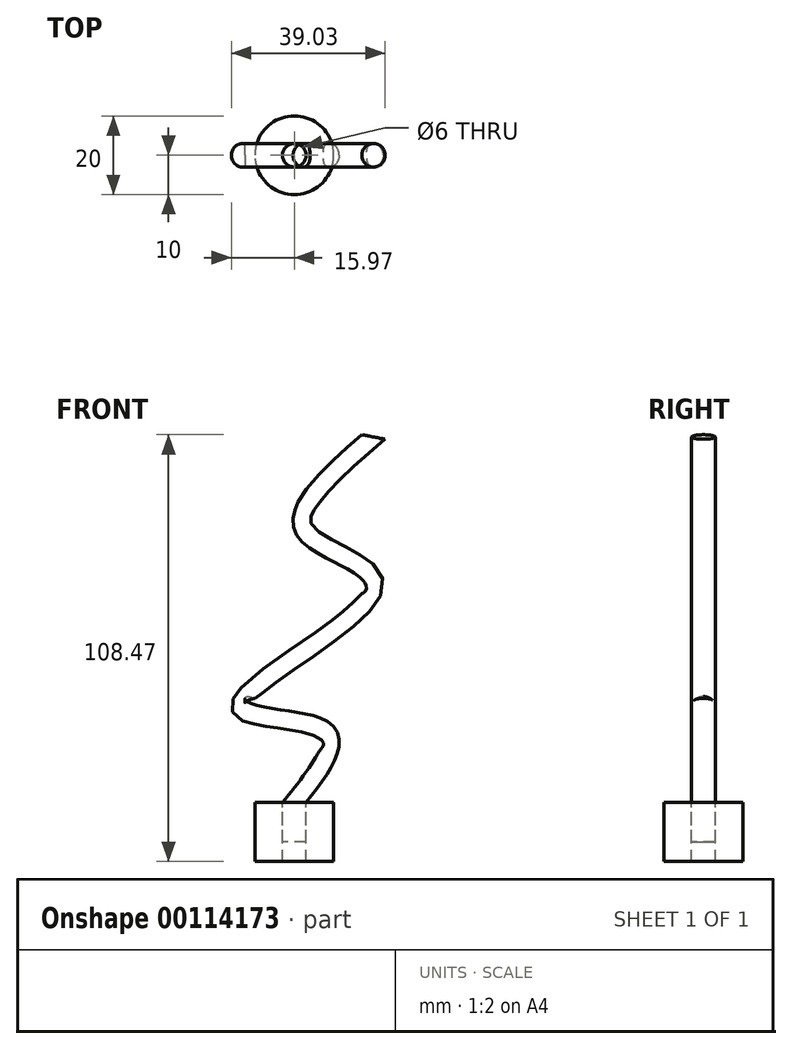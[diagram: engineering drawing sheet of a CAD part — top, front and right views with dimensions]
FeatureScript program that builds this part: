
annotation { "Feature Type Name" : "Feature", "Feature Type Description" : "" }
export const myFeature = defineFeature(function(context is Context, id is Id, definition is map)
    precondition{}
    {
        {
            var Q0;
            Q0=qCreatedBy(makeId("Top.planeOp"),FACE);
            var sketch = newSketch(context, id + "F0", { "sketchPlane" : qUnion([Q0])});
            skCircle(sketch, "E0", {"center": v(0, 0) * mm, "radius": 10 * mm});
            skCircle(sketch, "E1", {"center": v(0, 0) * mm, "radius": 3 * mm});
            skSolve(sketch);
        }
        {
            var Q0;
            Q0=qCreatedBy(makeId("Front.planeOp"),FACE);
            var sketch = newSketch(context, id + "F1", { "sketchPlane" : qUnion([Q0])});
            skFitSpline(sketch, "E2", {"points": [v(0, 0) * mm, v(7.33, 18.22) * mm, v(-13.25, 24.8) * mm, v(19.97, 54.7) * mm, v(3.1, 68.86) * mm, v(20.11, 92.9) * mm], "startDerivative": vector(102.5, 129.99) * mm, "endDerivative": vector(150.44, 129.38) * mm});
            skSolve(sketch);
        }
        {
            var Q0;
            Q0=makeQuery(id+"F0.imprint","IMPRINT",FACE,{"disambiguationData":[TD([[makeQuery(id+"F0.imprint","IMPRINT",EDGE,{"derivedFrom":sQuery(id+"F0.wireOp",EDGE,"E1")}),1.0]])]});
            var Q1;
            Q1=sQuery(id+"F1.wireOp",EDGE,"E2");
            sweep(context, id + "F2", {"profiles" : qUnion([Q0]), "path" : qUnion([Q1])});
        }
        {
            var Q0;
            Q0=makeQuery(id+"F0.imprint","IMPRINT",FACE,{"disambiguationData":[TD([[makeQuery(id+"F0.imprint","IMPRINT",EDGE,{"derivedFrom":sQuery(id+"F0.wireOp",EDGE,"E0")}),1.0]])]});
            extrude(context, id + "F3", {"entities" : qUnion([Q0]), "operationType" : NewBodyOperationType.ADD, "oppositeDirection" : true, "depth" : 15 * mm});
        }
        {
            var Q0;
            Q0=makeQuery(id+"F2.opSweep","CAP_FACE",FACE,{"disambiguationData":[OSD([sQuery(id+"F0.wireOp",EDGE,"E1"),sQuery(id+"F1.wireOp",VERTEX,"E2.start")])],"isStart":true});
            extrude(context, id + "F4", {"entities" : qUnion([Q0]), "depth" : 10 * mm});
        }
    });
